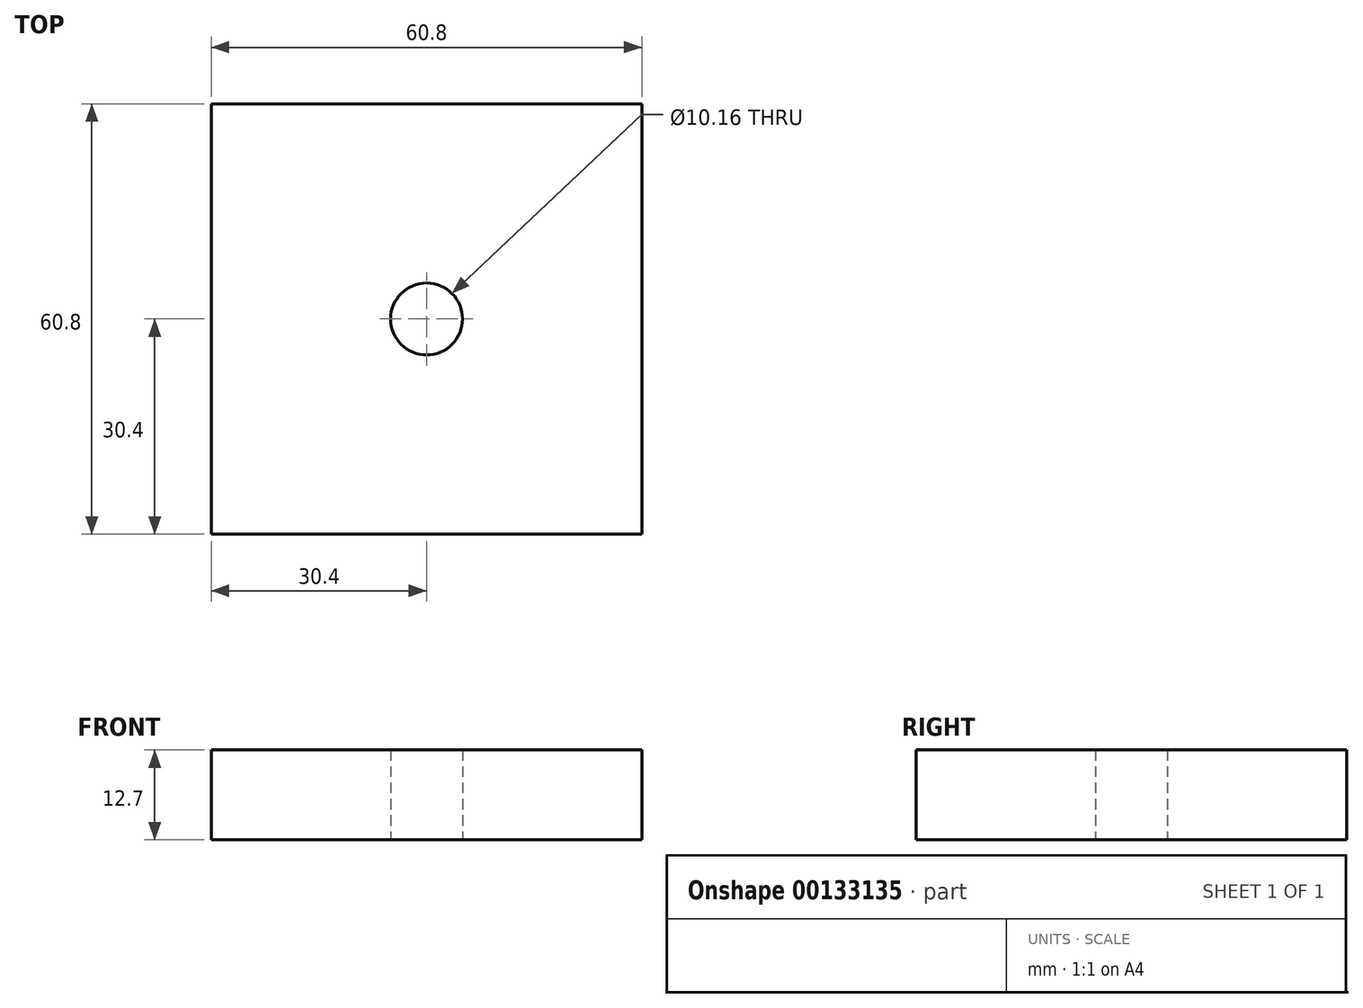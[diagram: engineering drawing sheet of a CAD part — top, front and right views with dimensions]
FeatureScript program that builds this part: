
annotation { "Feature Type Name" : "Feature", "Feature Type Description" : "" }
export const myFeature = defineFeature(function(context is Context, id is Id, definition is map)
    precondition{}
    {
        {
            var Q0;
            Q0=qCreatedBy(makeId("Top.planeOp"),FACE);
            var sketch = newSketch(context, id + "F0", { "sketchPlane" : qUnion([Q0])});
            skCircle(sketch, "E0", {"center": v(0, 0) * mm, "radius": 5.08 * mm});
            skLineSegment(sketch, "E1.bottom", {"start": v(30.4, 30.4) * mm, "end": v(-30.4, 30.4) * mm});
            skLineSegment(sketch, "E1.top", {"start": v(30.4, -30.4) * mm, "end": v(-30.4, -30.4) * mm});
            skLineSegment(sketch, "E1.left", {"start": v(30.4, 30.4) * mm, "end": v(30.4, -30.4) * mm});
            skLineSegment(sketch, "E1.right", {"start": v(-30.4, 30.4) * mm, "end": v(-30.4, -30.4) * mm});
            skSolve(sketch);
        }
        {
            var Q0;
            Q0=makeQuery(id+"F0.imprint","IMPRINT",FACE,{"disambiguationData":[TD([[makeQuery(id+"F0.imprint","IMPRINT",EDGE,{"derivedFrom":sQuery(id+"F0.wireOp",EDGE,"E0")}),-1.0]])]});
            extrude(context, id + "F1", {"entities" : qUnion([Q0]), "depth" : 12.7 * mm});
        }
    });
